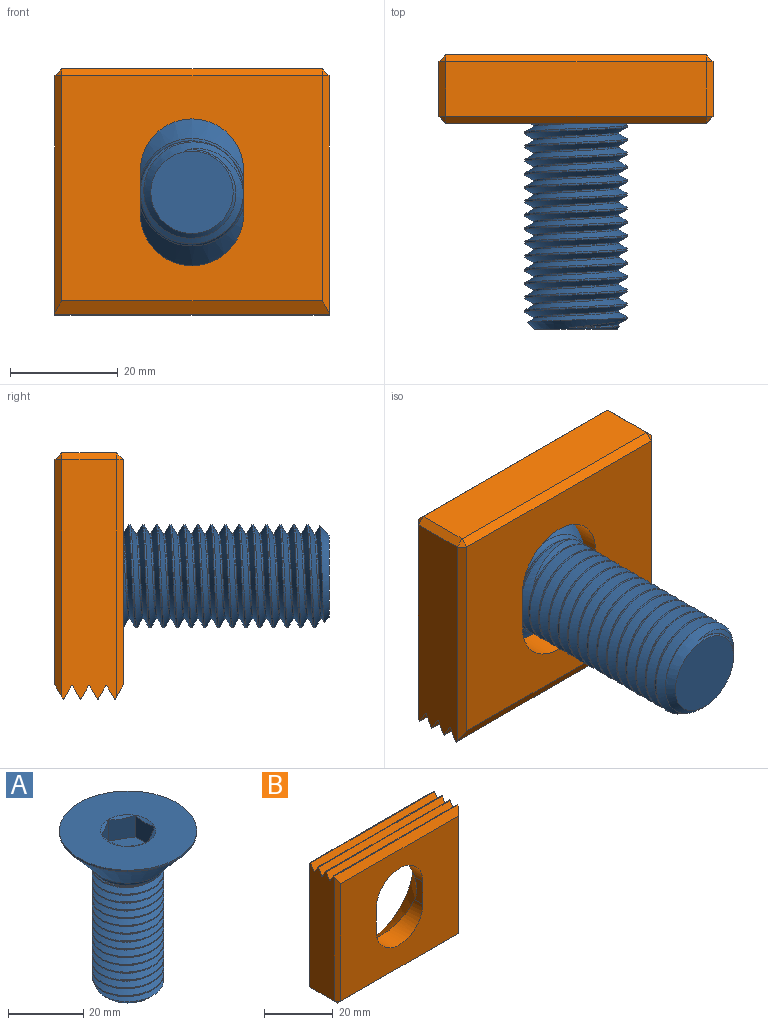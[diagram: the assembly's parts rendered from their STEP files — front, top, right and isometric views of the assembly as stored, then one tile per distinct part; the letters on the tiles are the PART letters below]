
ASSEMBLY  parts=2 mates=1
PART A: 24 faces, bbox 38.8x38.8x53.8 mm
  f0: cone r=7.33mm half-angle=60deg, axis (0,0,1), area 4.2mm2, adj f1,f13
  f1: plane 7.94x7.65mm, normal (-1,0,0), area 48.9mm2, adj f0,f2,f9,f11
  f2: plane 14.66x12.7mm, normal (0,0,1), area 139.7mm2, adj f1,f3,f5,f7,f9,f11
  f3: plane 9.31x8.62mm, normal (0.5,0.87,0), area 48.9mm2, adj f2,f4,f5,f11
  f4: cone r=7.33mm half-angle=60deg, axis (0,0,1), area 0mm2, adj f3,f13
  f5: plane 9.6x9.31mm, normal (1,0,0), area 48.9mm2, adj f2,f3,f6,f7
  f6: cone r=7.33mm half-angle=60deg, axis (0,0,1), area 0mm2, adj f5,f13
  f7: plane 9.31x8.62mm, normal (0.5,-0.87,0), area 48.9mm2, adj f2,f5,f8,f9
  f8: cone r=7.33mm half-angle=60deg, axis (0,0,1), area 0mm2, adj f7,f13
  f9: plane 9.31x8.62mm, normal (-0.5,-0.87,0), area 48.9mm2, adj f1,f2,f7,f10
  f10: cone r=7.33mm half-angle=60deg, axis (0,0,1), area 0mm2, adj f9,f13
  f11: plane 9.31x8.62mm, normal (-0.5,0.87,0), area 48.9mm2, adj f1,f2,f3,f12
  f12: cone r=7.33mm half-angle=60deg, axis (0,0,1), area 0mm2, adj f11,f13
  f13: plane 38.5x38.5mm, normal (0,0,1), area 878.9mm2, adj f0,f4,f6,f8,f10,f12,f14
  f14: cylinder r=18.26mm len=36.53mm, axis (0,0,1), area 57.7mm2, adj f13,f15
  f15: cone r=9.96mm half-angle=41deg, axis (0,0,1), area 1122.4mm2, adj f14,f16
  f16: torus R=11.28mm, axis (0,0,1), area 76.4mm2, adj f15,f17,f23
  f17: cylinder r=9.53mm len=37.68mm, axis (0,0,-1), area 281.9mm2, adj f16,f18,f21,f22
  f18: cone r=7.62mm half-angle=45deg, axis (0,0,1), area 79.8mm2, adj f17,f19,f20,f21,f22
  f19: plane 15.24x15.24mm, normal (0,0,-1), area 182.4mm2, adj f18
  f20: cylinder r=7.88mm len=37.74mm, axis (0,0,1), area 233.4mm2, adj f18,f21,f22,f23
  f21: bspline ~41.24x19.05mm, area 1547.3mm2, adj f17,f18,f20,f23
  f22: bspline ~39.33x19.01mm, area 1547.3mm2, adj f17,f18,f20,f23
  f23: cone r=9.53mm half-angle=46deg, axis (0,0,1), area 64.2mm2, adj f16,f20,f21,f22
PART B: 37 faces, bbox 50.8x12.7x45.7 mm
  f0: cone r=18.48mm half-angle=41deg, axis (0,1,0), area 961.7mm2, adj f1,f4,f7,f8,f9
  f1: cylinder r=9.58mm len=19.15mm, axis (0,1,0), area 157.4mm2, adj f0,f5,f7,f9
  f2: plane 44.41x10.18mm, normal (1,0,0), area 438.3mm2, adj f10,f11,f12,f13,f14,f15,f16,f17
  f3: plane 44.41x10.18mm, normal (-1,0,0), area 438.3mm2, adj f10,f11,f12,f13,f14,f15,f16,f17
  f4: plane 48.26x41.7mm, normal (0,1,0), area 939.7mm2, adj f0,f17,f25,f30,f31
  f5: plane 48.26x41.7mm, normal (0,-1,0), area 1570.7mm2, adj f1,f7,f8,f9,f10,f26,f32,f33
  f6: plane 48.26x10.16mm, normal (0,0,-1), area 490.3mm2, adj f27,f30,f33,f36
  f7: plane 8.03x3.39mm, normal (1,0,0), area 22.3mm2, adj f0,f1,f5,f8
  f8: cylinder r=9.58mm len=19.15mm, axis (0,1,0), area 157.4mm2, adj f0,f5,f7,f9
  f9: plane 8.03x3.39mm, normal (-1,0,0), area 22.2mm2, adj f0,f1,f5,f8
  f10: plane 50.8x2.56mm, normal (0,-0.87,0.5), area 146.9mm2, adj f2,f3,f5,f21,f26,f32
  f11: plane 50.8x2.37mm, normal (0,0.87,0.5), area 138.9mm2, adj f2,f3,f18,f21
  f12: plane 50.8x2.37mm, normal (0,-0.87,0.5), area 138.9mm2, adj f2,f3,f18,f22
  f13: plane 50.8x2.37mm, normal (0,0.87,0.5), area 138.9mm2, adj f2,f3,f19,f22
  f14: plane 50.8x2.37mm, normal (0,-0.87,0.5), area 138.9mm2, adj f2,f3,f19,f23
  f15: plane 50.8x2.37mm, normal (0,0.87,0.5), area 138.9mm2, adj f2,f3,f20,f23
  f16: plane 50.8x2.37mm, normal (0,-0.87,0.5), area 138.9mm2, adj f2,f3,f20,f24
  f17: plane 50.8x2.56mm, normal (0,0.87,0.5), area 146.9mm2, adj f2,f3,f4,f24,f25,f31
  f18: extruded ~50.8x0.22mm, area 15.5mm2, adj f2,f3,f11,f12
  f19: extruded ~50.8x0.22mm, area 15.5mm2, adj f2,f3,f13,f14
  f20: extruded ~50.8x0.22mm, area 15.5mm2, adj f2,f3,f15,f16
  f21: extruded ~50.8x0.22mm, area 15.5mm2, adj f2,f3,f10,f11
  f22: extruded ~50.8x0.22mm, area 15.5mm2, adj f2,f3,f12,f13
  f23: extruded ~50.8x0.22mm, area 15.5mm2, adj f2,f3,f14,f15
  f24: extruded ~50.8x0.22mm, area 15.5mm2, adj f2,f3,f16,f17
  f25: plane 43.9x1.27mm, normal (0.71,0.71,0), area 76.9mm2, adj f2,f4,f17,f28
  f26: plane 43.9x1.27mm, normal (0.71,-0.71,0), area 76.9mm2, adj f2,f5,f10,f29
  f27: plane 10.16x1.27mm, normal (0.71,0,-0.71), area 18.2mm2, adj f2,f6,f28,f29
  f28: plane 1.27x1.27mm, normal (0.58,0.58,-0.58), area 1.4mm2, adj f25,f27,f30
  f29: plane 1.27x1.27mm, normal (0.58,-0.58,-0.58), area 1.4mm2, adj f26,f27,f33
  f30: plane 48.26x1.27mm, normal (0,0.71,-0.71), area 86.7mm2, adj f4,f6,f28,f34
  f31: plane 43.9x1.27mm, normal (-0.71,0.71,0), area 76.9mm2, adj f3,f4,f17,f34
  f32: plane 43.9x1.27mm, normal (-0.71,-0.71,0), area 76.9mm2, adj f3,f5,f10,f35
  f33: plane 48.26x1.27mm, normal (0,-0.71,-0.71), area 86.7mm2, adj f5,f6,f29,f35
  f34: plane 1.27x1.27mm, normal (-0.58,0.58,-0.58), area 1.4mm2, adj f30,f31,f36
  f35: plane 1.27x1.27mm, normal (-0.58,-0.58,-0.58), area 1.4mm2, adj f32,f33,f36
  f36: plane 10.16x1.27mm, normal (-0.71,0,-0.71), area 18.2mm2, adj f3,f6,f34,f35
PLACE A rot(axis=(-1,0,0),90deg) t=(21.26,13.53,-114.52)mm fixed
PLACE B rot(axis=(0,1,0),180deg) t=(46.66,0.83,-137.38)mm
MATE pin_slot A.f0 <-> B.f0  axis (0,1,0) through (21.26,13.53,-114.52)mm
